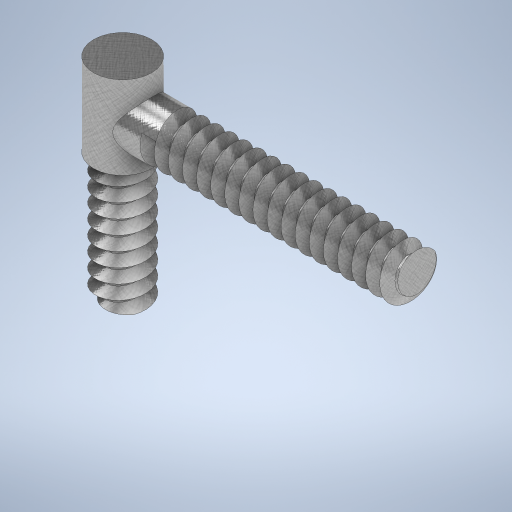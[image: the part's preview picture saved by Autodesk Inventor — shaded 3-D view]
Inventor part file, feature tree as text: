
AUTODESK INVENTOR PART (.ipt)
format: ipt  version: 2024 (Build 280153020, 153B)  size: 667,648 bytes
history: native  units: mm
features: sketch x5, extrude x3, helix x2, plane x2
ambient origin geometry x8: Origin, YZ Plane, XZ Plane, XY Plane, X Axis, Y Axis, Z Axis, Center Point
bodies: Solid1 (feature_tree)
feature tree (12):
  extrude  "Extrusion1"  Depth=1.7mm TaperAngle=0.0deg
  helix  "Coil1"  [1 undecoded]
  extrude  "Extrusion2"  Depth=0.2mm
  plane  "Work Plane1"
  extrude  "Extrusion4"  Depth=1.7mm
  plane  "Work Plane2"
  helix  "Coil3"  [1 undecoded]
  sketch  "Sketch1"  dims[d0=6.0mm d1=20.0mm d2=0.0mm d3=1.7mm]
  sketch  "Sketch2"  dims[d4=60.0deg d5=0.2mm]
  sketch  "Sketch4"  dims[d6=2.0mm]
  sketch  "Sketch8"  dims[d7=1.7mm d8=22.0mm d9=10.0mm d10=0.0mm d11=90.0deg d12=90.0deg d13=0.0mm d14=0.0mm d15=6.0mm d16=35.0mm d17=0.0mm]
  sketch  "Sketch9"  dims[d28=23.0mm d42=7.0mm d43=10.0mm d44=0.0mm d45=0.0mm d46=1.7mm d47=60.0deg d48=0.2mm d49=2.0mm d50=1.7mm d51=32.0mm d52=10.0mm d53=0.0mm d54=90.0deg d55=90.0deg d56=0.0mm d57=0.0mm]
note: 2 required parameter values undecoded (feature->parameter linkage not recoverable at this tier; creation-order binding heuristic only, values carry confidence <= 0.55)
